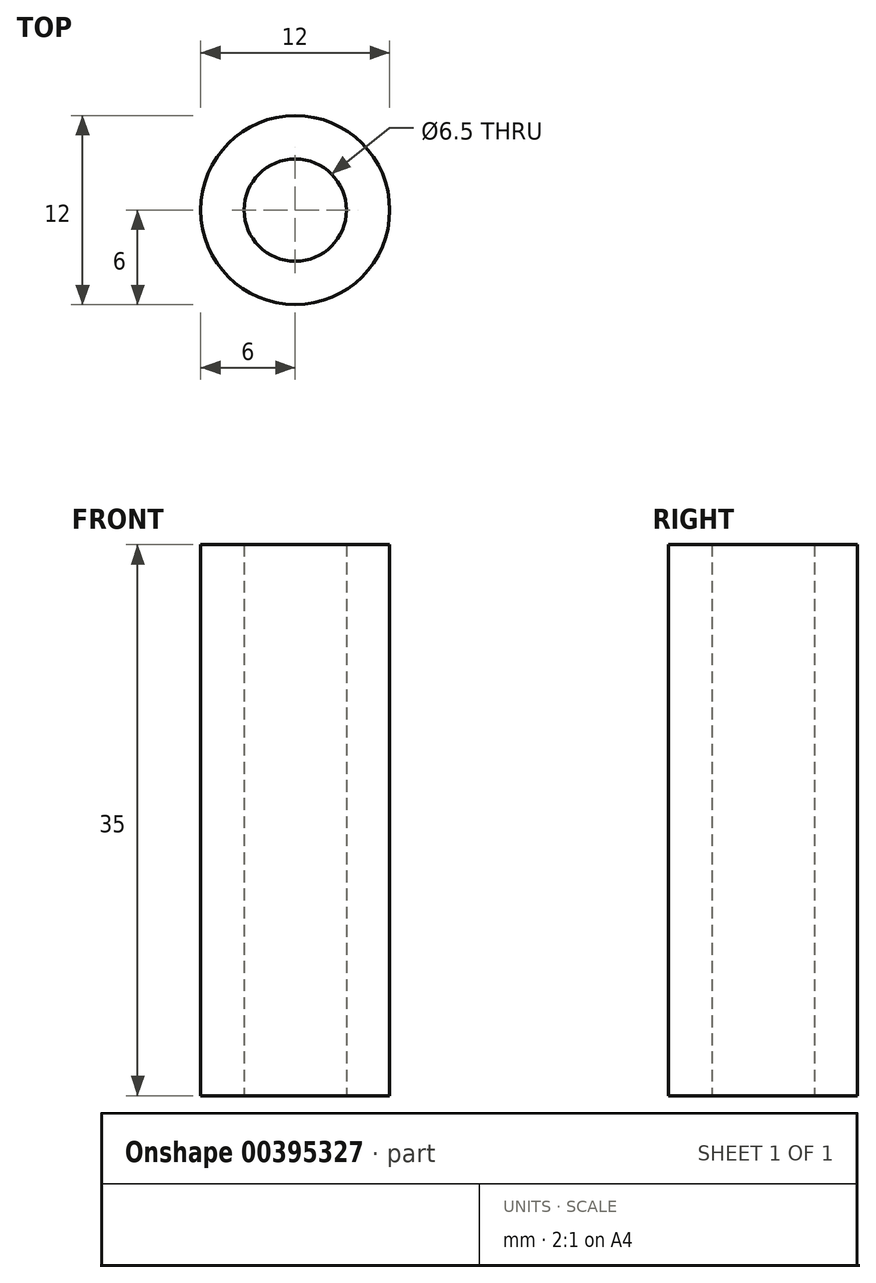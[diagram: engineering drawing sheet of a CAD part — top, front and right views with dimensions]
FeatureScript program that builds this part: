
annotation { "Feature Type Name" : "Feature", "Feature Type Description" : "" }
export const myFeature = defineFeature(function(context is Context, id is Id, definition is map)
    precondition{}
    {
        {
            var Q0;
            Q0=qCreatedBy(makeId("Top.planeOp"),FACE);
            var sketch = newSketch(context, id + "F0", { "sketchPlane" : qUnion([Q0])});
            skCircle(sketch, "E0", {"center": v(0, 0) * mm, "radius": 6 * mm});
            skCircle(sketch, "E1", {"center": v(0, 0) * mm, "radius": 3.25 * mm});
            skSolve(sketch);
        }
        {
            var Q0;
            Q0=qSketchRegion(id+"F0",true);
            extrude(context, id + "F1", {"entities" : qUnion([Q0]), "depth" : 35 * mm});
        }
    });
